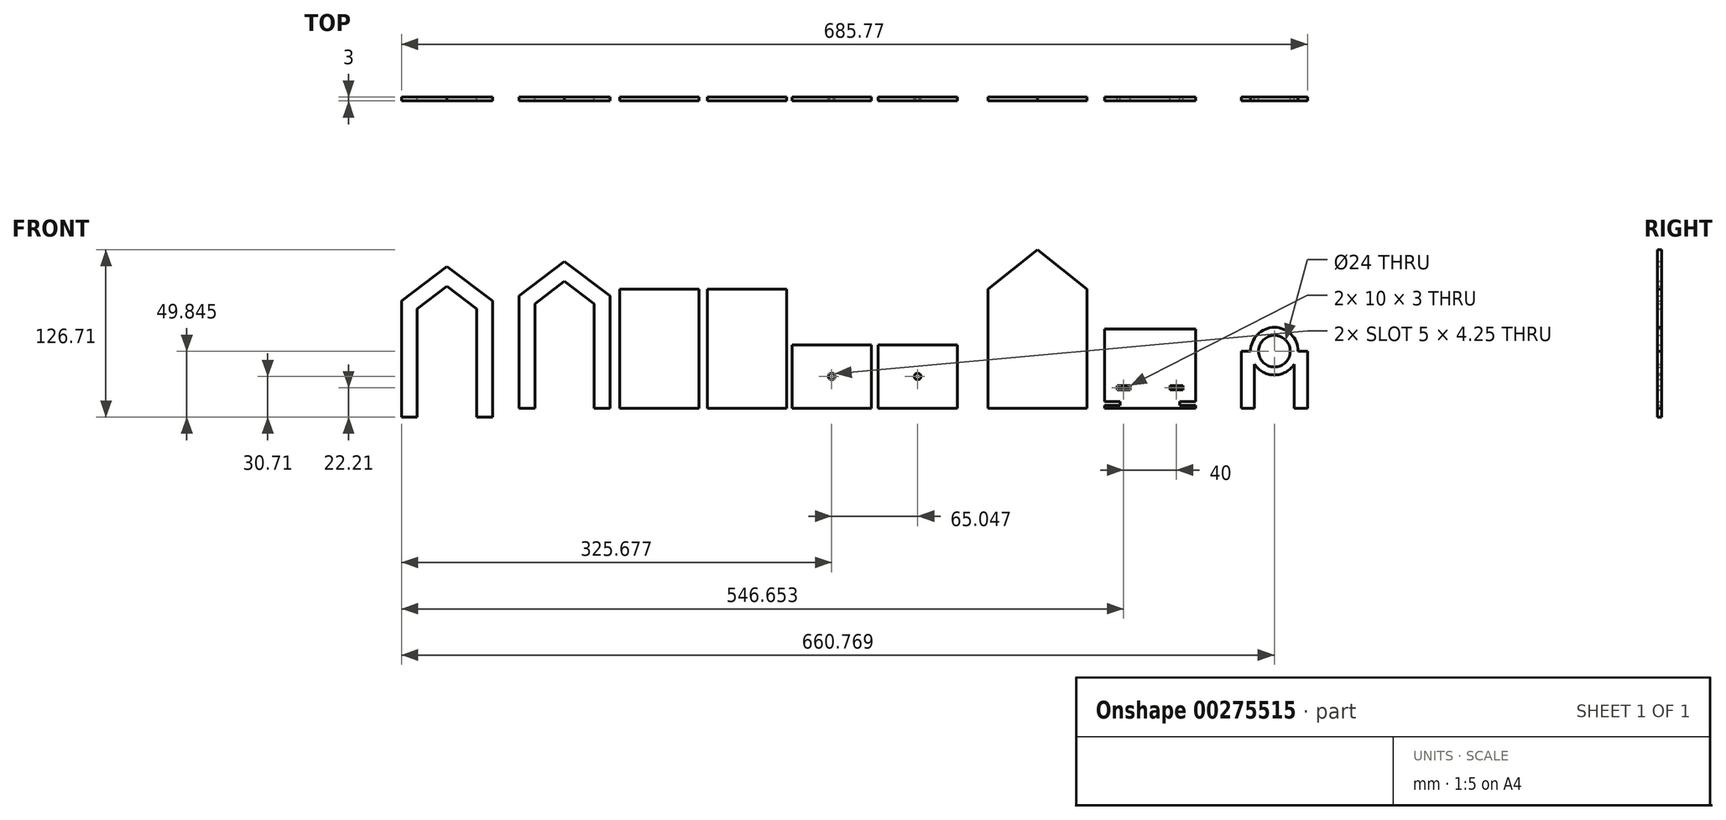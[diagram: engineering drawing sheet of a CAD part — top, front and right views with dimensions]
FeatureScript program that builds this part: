
annotation { "Feature Type Name" : "Feature", "Feature Type Description" : "" }
export const myFeature = defineFeature(function(context is Context, id is Id, definition is map)
    precondition{}
    {
        {
            var Q0;
            Q0=qCreatedBy(makeId("Front.planeOp"),FACE);
            var sketch = newSketch(context, id + "F0", { "sketchPlane" : qUnion([Q0])});
            skLineSegment(sketch, "E0.bottom", {"start": v(0, 0) * mm, "end": v(12, 0) * mm});
            skLineSegment(sketch, "E0.left", {"start": v(0, 0) * mm, "end": v(0, 85) * mm});
            skLineSegment(sketch, "E0.right", {"start": v(69, 0) * mm, "end": v(69, 85) * mm});
            skLineSegment(sketch, "E1", {"start": v(34.5, 85) * mm, "end": v(34.5, 144.96) * mm, "construction": true});
            skLineSegment(sketch, "E2", {"start": v(0, 85) * mm, "end": v(34.5, 111) * mm});
            skLineSegment(sketch, "E3", {"start": v(34.5, 111) * mm, "end": v(69, 85) * mm});
            skLineSegment(sketch, "E4.0", {"start": v(57, 0) * mm, "end": v(57, 79.02) * mm});
            skLineSegment(sketch, "E4.1", {"start": v(34.5, 95.97) * mm, "end": v(57, 79.02) * mm});
            skLineSegment(sketch, "E4.3", {"start": v(12, 0) * mm, "end": v(12, 79.02) * mm});
            skLineSegment(sketch, "E4.4", {"start": v(12, 79.02) * mm, "end": v(34.5, 95.97) * mm});
            skLineSegment(sketch, "E5.trimOffspring", {"start": v(57, 0) * mm, "end": v(69, 0) * mm});
            skLineSegment(sketch, "E6.left", {"start": v(-88.93, -3.7) * mm, "end": v(-88.93, 81.3) * mm});
            skLineSegment(sketch, "E6.right", {"start": v(-19.93, -4.61) * mm, "end": v(-19.93, 81.3) * mm});
            skLineSegment(sketch, "E7", {"start": v(-88.93, 81.3) * mm, "end": v(-54.43, 107.3) * mm});
            skLineSegment(sketch, "E8", {"start": v(-54.43, 107.3) * mm, "end": v(-19.93, 81.3) * mm});
            skLineSegment(sketch, "E9.0", {"start": v(-31.93, -3.7) * mm, "end": v(-31.93, 75.3) * mm});
            skLineSegment(sketch, "E9.1", {"start": v(-54.43, 92.26) * mm, "end": v(-31.93, 75.3) * mm});
            skLineSegment(sketch, "E9.3", {"start": v(-76.93, -4.61) * mm, "end": v(-76.93, 75.3) * mm});
            skLineSegment(sketch, "E9.4", {"start": v(-76.93, 75.3) * mm, "end": v(-54.43, 92.26) * mm});
            skLineSegment(sketch, "E10.top", {"start": v(-88.93, -6.7) * mm, "end": v(-76.93, -6.7) * mm});
            skLineSegment(sketch, "E10.left", {"start": v(-88.93, -3.7) * mm, "end": v(-88.93, -6.7) * mm});
            skLineSegment(sketch, "E10.right", {"start": v(-76.93, -3.7) * mm, "end": v(-76.93, -6.7) * mm});
            skLineSegment(sketch, "E11.top", {"start": v(-31.93, -6.7) * mm, "end": v(-19.93, -6.7) * mm});
            skLineSegment(sketch, "E11.left", {"start": v(-31.93, -3.7) * mm, "end": v(-31.93, -6.7) * mm});
            skLineSegment(sketch, "E11.right", {"start": v(-19.93, -4.61) * mm, "end": v(-19.93, -6.7) * mm});
            skSolve(sketch);
        }
        {
            var Q0;
            Q0 = qSketchRegion(id + "F0", true);
            extrude(context, id + "F1", {"entities" : qUnion([Q0]), "depth" : 3 * mm});
        }
        {
            var Q0;
            Q0=qCreatedBy(makeId("Front.planeOp"),FACE);
            var sketch = newSketch(context, id + "F2", { "sketchPlane" : qUnion([Q0])});
            skLineSegment(sketch, "E12.bottom", {"start": v(76.18, 0) * mm, "end": v(136.18, 0) * mm});
            skLineSegment(sketch, "E12.top", {"start": v(76.18, 90) * mm, "end": v(136.18, 90) * mm});
            skLineSegment(sketch, "E12.left", {"start": v(76.18, 0) * mm, "end": v(76.18, 90) * mm});
            skLineSegment(sketch, "E12.right", {"start": v(136.18, 0) * mm, "end": v(136.18, 90) * mm});
            skLineSegment(sketch, "E13.bottom", {"start": v(142.58, 0) * mm, "end": v(202.58, 0) * mm});
            skLineSegment(sketch, "E13.top", {"start": v(142.58, 90) * mm, "end": v(202.58, 90) * mm});
            skLineSegment(sketch, "E13.left", {"start": v(142.58, 0) * mm, "end": v(142.58, 90) * mm});
            skLineSegment(sketch, "E13.right", {"start": v(202.58, 0) * mm, "end": v(202.58, 90) * mm});
            skLineSegment(sketch, "E14.bottom", {"start": v(206.75, 0) * mm, "end": v(266.75, 0) * mm});
            skLineSegment(sketch, "E14.top", {"start": v(206.75, 48) * mm, "end": v(266.75, 48) * mm});
            skLineSegment(sketch, "E14.left", {"start": v(206.75, 0) * mm, "end": v(206.75, 48) * mm});
            skLineSegment(sketch, "E14.right", {"start": v(266.75, 0) * mm, "end": v(266.75, 48) * mm});
            skLineSegment(sketch, "E15.bottom", {"start": v(271.8, 0) * mm, "end": v(331.8, 0) * mm});
            skLineSegment(sketch, "E15.top", {"start": v(271.8, 48) * mm, "end": v(331.8, 48) * mm});
            skLineSegment(sketch, "E15.left", {"start": v(271.8, 0) * mm, "end": v(271.8, 48) * mm});
            skLineSegment(sketch, "E15.right", {"start": v(331.8, 0) * mm, "end": v(331.8, 48) * mm});
            skLineSegment(sketch, "E16.bottom", {"start": v(354.92, 0) * mm, "end": v(429.92, 0) * mm});
            skLineSegment(sketch, "E16.left", {"start": v(354.92, 0) * mm, "end": v(354.92, 90) * mm});
            skLineSegment(sketch, "E16.right", {"start": v(429.92, 0) * mm, "end": v(429.92, 90) * mm});
            skLineSegment(sketch, "E17", {"start": v(354.92, 90) * mm, "end": v(392.42, 120) * mm});
            skLineSegment(sketch, "E18", {"start": v(392.42, 120) * mm, "end": v(429.92, 90) * mm});
            skLineSegment(sketch, "E19.bottom", {"start": v(443.22, 0) * mm, "end": v(512.22, 0) * mm});
            skLineSegment(sketch, "E19.top", {"start": v(443.22, 60) * mm, "end": v(512.22, 60) * mm});
            skLineSegment(sketch, "E19.left", {"start": v(443.22, 0) * mm, "end": v(443.22, 2) * mm});
            skLineSegment(sketch, "E19.right", {"start": v(512.22, 0) * mm, "end": v(512.22, 2) * mm});
            skArc(sketch, "E20", {"start": v(556.84, 33.18) * mm, "mid": v(571.84, 25.13) * mm, "end": v(586.84, 33.18) * mm});
            skCircle(sketch, "E21", {"center": v(571.84, 43.13) * mm, "radius": 12 * mm});
            skLineSegment(sketch, "E22.bottom", {"start": v(589.84, 43.13) * mm, "end": v(596.84, 43.13) * mm});
            skLineSegment(sketch, "E22.top", {"start": v(586.84, 0) * mm, "end": v(596.84, 0) * mm});
            skLineSegment(sketch, "E22.left", {"start": v(586.84, 33.18) * mm, "end": v(586.84, 0) * mm});
            skLineSegment(sketch, "E22.right", {"start": v(596.84, 43.13) * mm, "end": v(596.84, 0) * mm});
            skPoint(sketch, "E23.oppositeSnap0", {"position": v(591.84, 0) * mm});
            skLineSegment(sketch, "E23.bottom", {"start": v(553.84, 43.13) * mm, "end": v(546.84, 43.13) * mm});
            skLineSegment(sketch, "E23.top", {"start": v(556.84, 0) * mm, "end": v(546.84, 0) * mm});
            skLineSegment(sketch, "E23.left", {"start": v(556.84, 33.18) * mm, "end": v(556.84, 0) * mm});
            skLineSegment(sketch, "E23.right", {"start": v(546.84, 43.13) * mm, "end": v(546.84, 0) * mm});
            skPoint(sketch, "E24.orphan", {"position": v(556.84, 43.13) * mm});
            skPoint(sketch, "E25.orphan", {"position": v(586.84, 43.13) * mm});
            skArc(sketch, "E26.trimOffspring", {"start": v(589.84, 43.13) * mm, "mid": v(571.84, 61.13) * mm, "end": v(553.84, 43.13) * mm});
            skLineSegment(sketch, "E27.bottom", {"start": v(452.72, 17) * mm, "end": v(462.72, 17) * mm});
            skLineSegment(sketch, "E27.top", {"start": v(452.72, 14) * mm, "end": v(462.72, 14) * mm});
            skLineSegment(sketch, "E27.left", {"start": v(452.72, 17) * mm, "end": v(452.72, 14) * mm});
            skLineSegment(sketch, "E27.right", {"start": v(462.72, 17) * mm, "end": v(462.72, 14) * mm});
            skLineSegment(sketch, "E28", {"start": v(477.72, 0) * mm, "end": v(477.72, 27.45) * mm, "construction": true});
            skLineSegment(sketch, "E29", {"start": v(477.72, 27.45) * mm, "end": v(468.88, 32.77) * mm, "construction": true});
            skLineSegment(sketch, "E30.MirrorCS", {"start": v(502.72, 17) * mm, "end": v(492.72, 17) * mm});
            skLineSegment(sketch, "E31.MirrorCS", {"start": v(502.72, 14) * mm, "end": v(492.72, 14) * mm});
            skLineSegment(sketch, "E32.MirrorCS", {"start": v(502.72, 17) * mm, "end": v(502.72, 14) * mm});
            skLineSegment(sketch, "E33.MirrorCS", {"start": v(492.72, 17) * mm, "end": v(492.72, 14) * mm});
            skLineSegment(sketch, "E34.bottom", {"start": v(443.22, 5) * mm, "end": v(455.22, 5) * mm});
            skLineSegment(sketch, "E34.top", {"start": v(443.22, 2) * mm, "end": v(455.22, 2) * mm});
            skLineSegment(sketch, "E34.right", {"start": v(455.22, 5) * mm, "end": v(455.22, 2) * mm});
            skLineSegment(sketch, "E35.MirrorCS", {"start": v(512.22, 5) * mm, "end": v(500.22, 5) * mm});
            skLineSegment(sketch, "E36.MirrorCS", {"start": v(500.22, 5) * mm, "end": v(500.22, 2) * mm});
            skLineSegment(sketch, "E37.MirrorCS", {"start": v(512.22, 2) * mm, "end": v(500.22, 2) * mm});
            skLineSegment(sketch, "E38.trimOffspring", {"start": v(512.22, 5) * mm, "end": v(512.22, 60) * mm});
            skLineSegment(sketch, "E39.trimOffspring", {"start": v(443.22, 5) * mm, "end": v(443.22, 60) * mm});
            skArc(sketch, "E40", {"start": v(300.48, 26.13) * mm, "mid": v(299.3, 24) * mm, "end": v(300.48, 21.88) * mm});
            skLineSegment(sketch, "E41", {"start": v(301.8, 48) * mm, "end": v(301.8, 0) * mm, "construction": true});
            skLineSegment(sketch, "E42", {"start": v(271.8, 24) * mm, "end": v(331.8, 24) * mm, "construction": true});
            skLineSegment(sketch, "E43", {"start": v(300.48, 26.12) * mm, "end": v(303.11, 26.12) * mm});
            skLineSegment(sketch, "E44", {"start": v(300.48, 21.88) * mm, "end": v(303.11, 21.88) * mm});
            skArc(sketch, "E45.trimOffspring", {"start": v(303.11, 21.88) * mm, "mid": v(304.3, 24) * mm, "end": v(303.11, 26.13) * mm});
            skLineSegment(sketch, "E46", {"start": v(236.75, 48) * mm, "end": v(236.75, 0) * mm, "construction": true});
            skArc(sketch, "E47", {"start": v(238.06, 21.87) * mm, "mid": v(239.25, 24) * mm, "end": v(238.06, 26.13) * mm});
            skLineSegment(sketch, "E48", {"start": v(235.43, 26.12) * mm, "end": v(238.06, 26.12) * mm});
            skLineSegment(sketch, "E49", {"start": v(235.43, 21.88) * mm, "end": v(238.06, 21.88) * mm});
            skArc(sketch, "E50.trimOffspring", {"start": v(235.43, 26.12) * mm, "mid": v(234.25, 24) * mm, "end": v(235.43, 21.88) * mm});
            skSolve(sketch);
        }
        {
            var Q0;
            Q0 = qSketchRegion(id + "F2", true);
            extrude(context, id + "F3", {"entities" : qUnion([Q0]), "depth" : 3 * mm});
        }
    });
